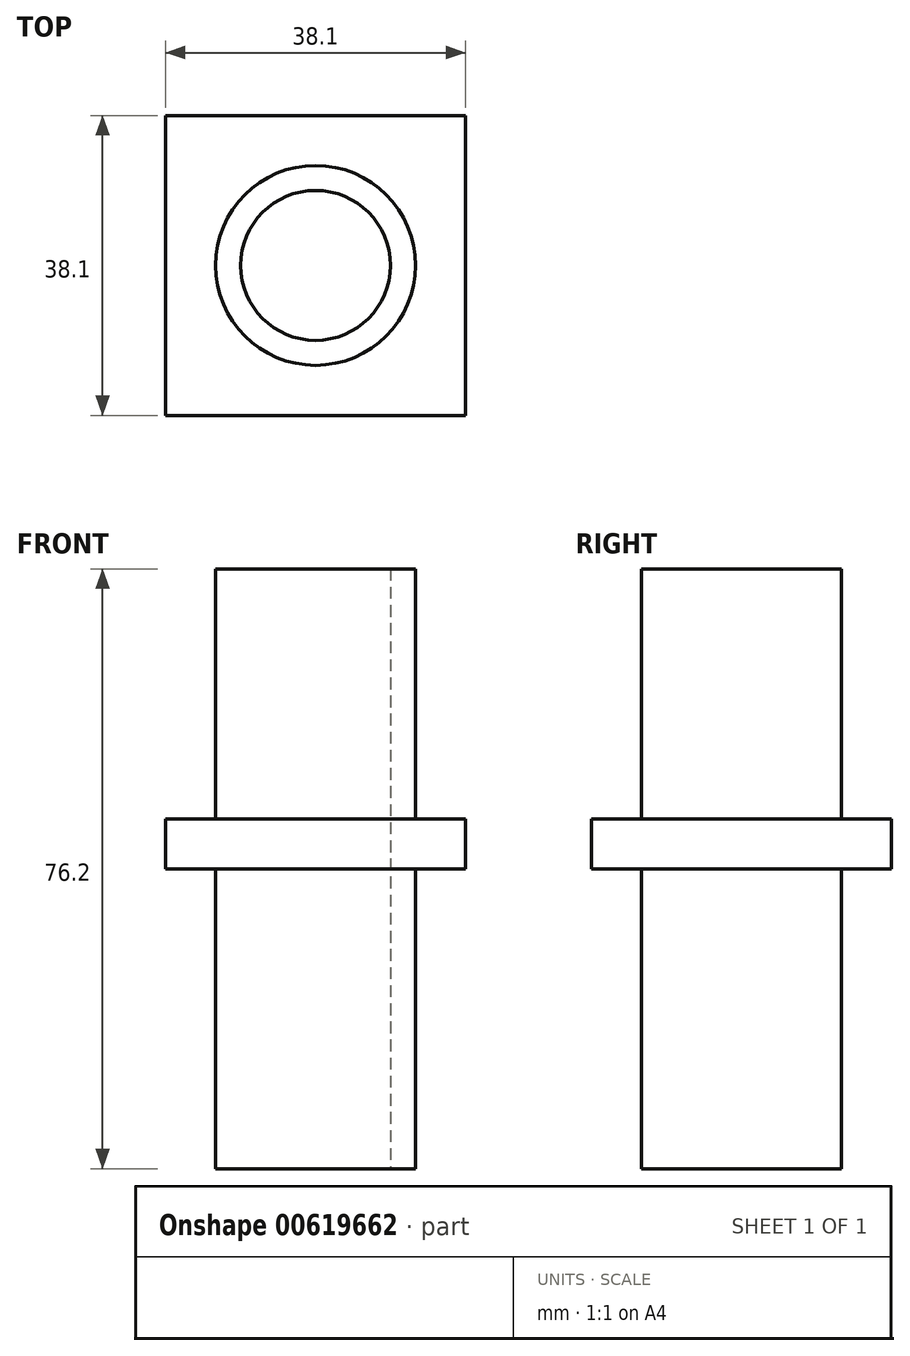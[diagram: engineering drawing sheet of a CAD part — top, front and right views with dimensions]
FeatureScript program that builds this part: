
annotation { "Feature Type Name" : "Feature", "Feature Type Description" : "" }
export const myFeature = defineFeature(function(context is Context, id is Id, definition is map)
    precondition{}
    {
        {
            var Q0;
            Q0=qCreatedBy(makeId("Top.planeOp"),FACE);
            var sketch = newSketch(context, id + "F0", { "sketchPlane" : qUnion([Q0])});
            skCircle(sketch, "E0", {"center": v(0, 0) * mm, "radius": 12.7 * mm});
            skCircle(sketch, "E1", {"center": v(0, 0) * mm, "radius": 9.53 * mm});
            skSolve(sketch);
        }
        {
            var Q0;
            Q0 = qSketchRegion(id + "F0", true);
            extrude(context, id + "F1", {"entities" : qUnion([Q0]), "depth" : 38.1 * mm, "offsetDistance" : 25.4 * mm});
        }
        {
            var Q0;
            Q0=qCreatedBy(makeId("Top.planeOp"),FACE);
            var sketch = newSketch(context, id + "F2", { "sketchPlane" : qUnion([Q0])});
            skLineSegment(sketch, "E2.bottom", {"start": v(-19.05, 19.05) * mm, "end": v(19.05, 19.05) * mm});
            skLineSegment(sketch, "E2.top", {"start": v(-19.05, -19.05) * mm, "end": v(19.05, -19.05) * mm});
            skLineSegment(sketch, "E2.left", {"start": v(-19.05, 19.05) * mm, "end": v(-19.05, -19.05) * mm});
            skLineSegment(sketch, "E2.right", {"start": v(19.05, 19.05) * mm, "end": v(19.05, -19.05) * mm});
            skCircle(sketch, "E3", {"center": v(0, 0) * mm, "radius": 9.53 * mm});
            skSolve(sketch);
        }
        {
            var Q0;
            Q0=makeQuery(id+"F2.imprint","IMPRINT",FACE,{"disambiguationData":[TD([[makeQuery(id+"F2.imprint","IMPRINT",EDGE,{"derivedFrom":sQuery(id+"F2.wireOp",EDGE,"E2.bottom")}),-1.0]])]});
            extrude(context, id + "F3", {"entities" : qUnion([Q0]), "operationType" : NewBodyOperationType.ADD, "depth" : 6.35 * mm, "offsetDistance" : 25.4 * mm});
        }
        {
            var Q0;
            Q0=makeQuery(id+"F3.boolean.opBoolean","MERGE",FACE,{"derivedFrom":[makeQuery(id+"F1.opExtrude","CAP_FACE",FACE,{"disambiguationData":[OSD([sQuery(id+"F0.wireOp",EDGE,"E0"),sQuery(id+"F0.wireOp",EDGE,"E1")])],"isStart":true}),makeQuery(id+"F3.opExtrude","CAP_FACE",FACE,{"disambiguationData":[OSD([sQuery(id+"F2.wireOp",EDGE,"E2.bottom"),sQuery(id+"F2.wireOp",EDGE,"E2.top"),sQuery(id+"F2.wireOp",EDGE,"E2.left"),sQuery(id+"F2.wireOp",EDGE,"E2.right"),sQuery(id+"F2.wireOp",EDGE,"E3")])],"isStart":true})]});
            var sketch = newSketch(context, id + "F4", { "sketchPlane" : qUnion([Q0])});
            skCircle(sketch, "E4", {"center": v(0, 0) * mm, "radius": 9.52 * mm});
            skCircle(sketch, "E5", {"center": v(0, 0) * mm, "radius": 12.7 * mm});
            skSolve(sketch);
        }
        {
            var Q0;
            Q0=makeQuery(id+"F4.imprint","IMPRINT",FACE,{"disambiguationData":[TD([[makeQuery(id+"F4.imprint","IMPRINT",EDGE,{"derivedFrom":sQuery(id+"F4.wireOp",EDGE,"E4")}),1.0]])]});
            extrude(context, id + "F5", {"entities" : qUnion([Q0]), "operationType" : NewBodyOperationType.ADD, "depth" : 38.1 * mm, "offsetDistance" : 25.4 * mm});
        }
    });
